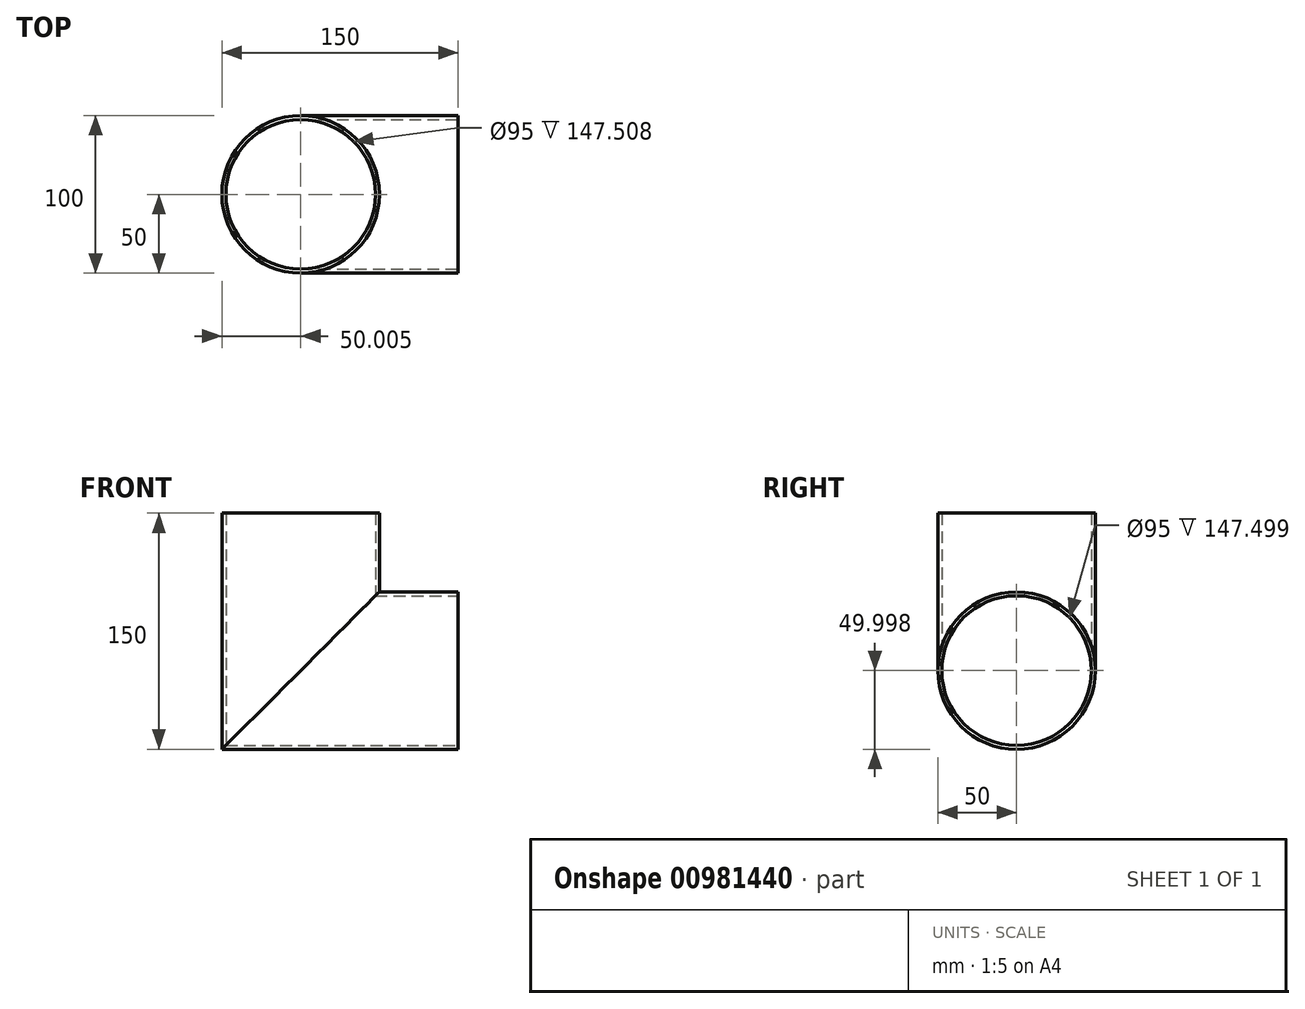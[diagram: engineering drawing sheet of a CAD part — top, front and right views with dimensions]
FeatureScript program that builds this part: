
annotation { "Feature Type Name" : "Feature", "Feature Type Description" : "" }
export const myFeature = defineFeature(function(context is Context, id is Id, definition is map)
    precondition{}
    {
        {
            var Q0;
            Q0=qCreatedBy(makeId("Front.planeOp"),FACE);
            var sketch = newSketch(context, id + "F0", { "sketchPlane" : qUnion([Q0])});
            skLineSegment(sketch, "E0", {"start": v(-88.47, 70.59) * mm, "end": v(11.53, 70.59) * mm});
            skLineSegment(sketch, "E1", {"start": v(11.53, 70.59) * mm, "end": v(11.53, 20.59) * mm});
            skLineSegment(sketch, "E2", {"start": v(11.53, 20.59) * mm, "end": v(61.53, 20.59) * mm});
            skLineSegment(sketch, "E3", {"start": v(61.53, 20.59) * mm, "end": v(61.53, -79.41) * mm});
            skLineSegment(sketch, "E4", {"start": v(-88.47, 70.59) * mm, "end": v(-88.47, -79.41) * mm});
            skLineSegment(sketch, "E5", {"start": v(-88.47, -79.41) * mm, "end": v(61.53, -79.41) * mm});
            skSolve(sketch);
        }
        {
            var Q0;
            Q0=makeQuery(id+"F0.imprint","IMPRINT",FACE,{"disambiguationData":[TD([[makeQuery(id+"F0.imprint","IMPRINT",EDGE,{"derivedFrom":sQuery(id+"F0.wireOp",EDGE,"E0")}),-1.0]])]});
            extrude(context, id + "F1", {"entities" : qUnion([Q0]), "depth" : 100 * mm, "offsetDistance" : 25 * mm});
        }
        {
            var Q0;
            Q0=makeQuery(id+"F1.opExtrude","CAP_EDGE",EDGE,{"disambiguationData":[OSD([sQuery(id+"F0.wireOp",EDGE,"E5")])],"isStart":false});
            var Q1;
            Q1=makeQuery(id+"F1.opExtrude","CAP_EDGE",EDGE,{"disambiguationData":[OSD([sQuery(id+"F0.wireOp",EDGE,"E5")])],"isStart":true});
            var Q2;
            Q2=makeQuery(id+"F1.opExtrude","CAP_EDGE",EDGE,{"disambiguationData":[OSD([sQuery(id+"F0.wireOp",EDGE,"E2")])],"isStart":false});
            var Q3;
            Q3=makeQuery(id+"F1.opExtrude","CAP_EDGE",EDGE,{"disambiguationData":[OSD([sQuery(id+"F0.wireOp",EDGE,"E2")])],"isStart":true});
            var Q4;
            Q4=makeQuery(id+"F1.opExtrude","CAP_EDGE",EDGE,{"disambiguationData":[OSD([sQuery(id+"F0.wireOp",EDGE,"E1")])],"isStart":true});
            var Q5;
            Q5=makeQuery(id+"F1.opExtrude","CAP_EDGE",EDGE,{"disambiguationData":[OSD([sQuery(id+"F0.wireOp",EDGE,"E1")])],"isStart":false});
            var Q6;
            Q6=makeQuery(id+"F1.opExtrude","CAP_EDGE",EDGE,{"disambiguationData":[OSD([sQuery(id+"F0.wireOp",EDGE,"E4")])],"isStart":false});
            var Q7;
            Q7=makeQuery(id+"F1.opExtrude","CAP_EDGE",EDGE,{"disambiguationData":[OSD([sQuery(id+"F0.wireOp",EDGE,"E4")])],"isStart":true});
            fillet(context, id + "F2", {"entities" : qUnion([Q0, Q1, Q2, Q3, Q4, Q5, Q6, Q7]), "tangentPropagation" : true, "radius" : 50 * mm, "defaultsChanged" : false, "vertexSettings" : [], "allowEdgeOverflow" : false});
        }
        {
            var Q0;
            Q0=makeQuery(id+"F1.opExtrude","SWEPT_FACE",FACE,{"disambiguationData":[OSD([sQuery(id+"F0.wireOp",EDGE,"E3")])]});
            var Q1;
            Q1=makeQuery(id+"F1.opExtrude","SWEPT_FACE",FACE,{"disambiguationData":[OSD([sQuery(id+"F0.wireOp",EDGE,"E0")])]});
            shell(context, id + "F3", {"entities" : qUnion([Q0, Q1]), "thickness" : 2.5 * mm});
        }
    });
